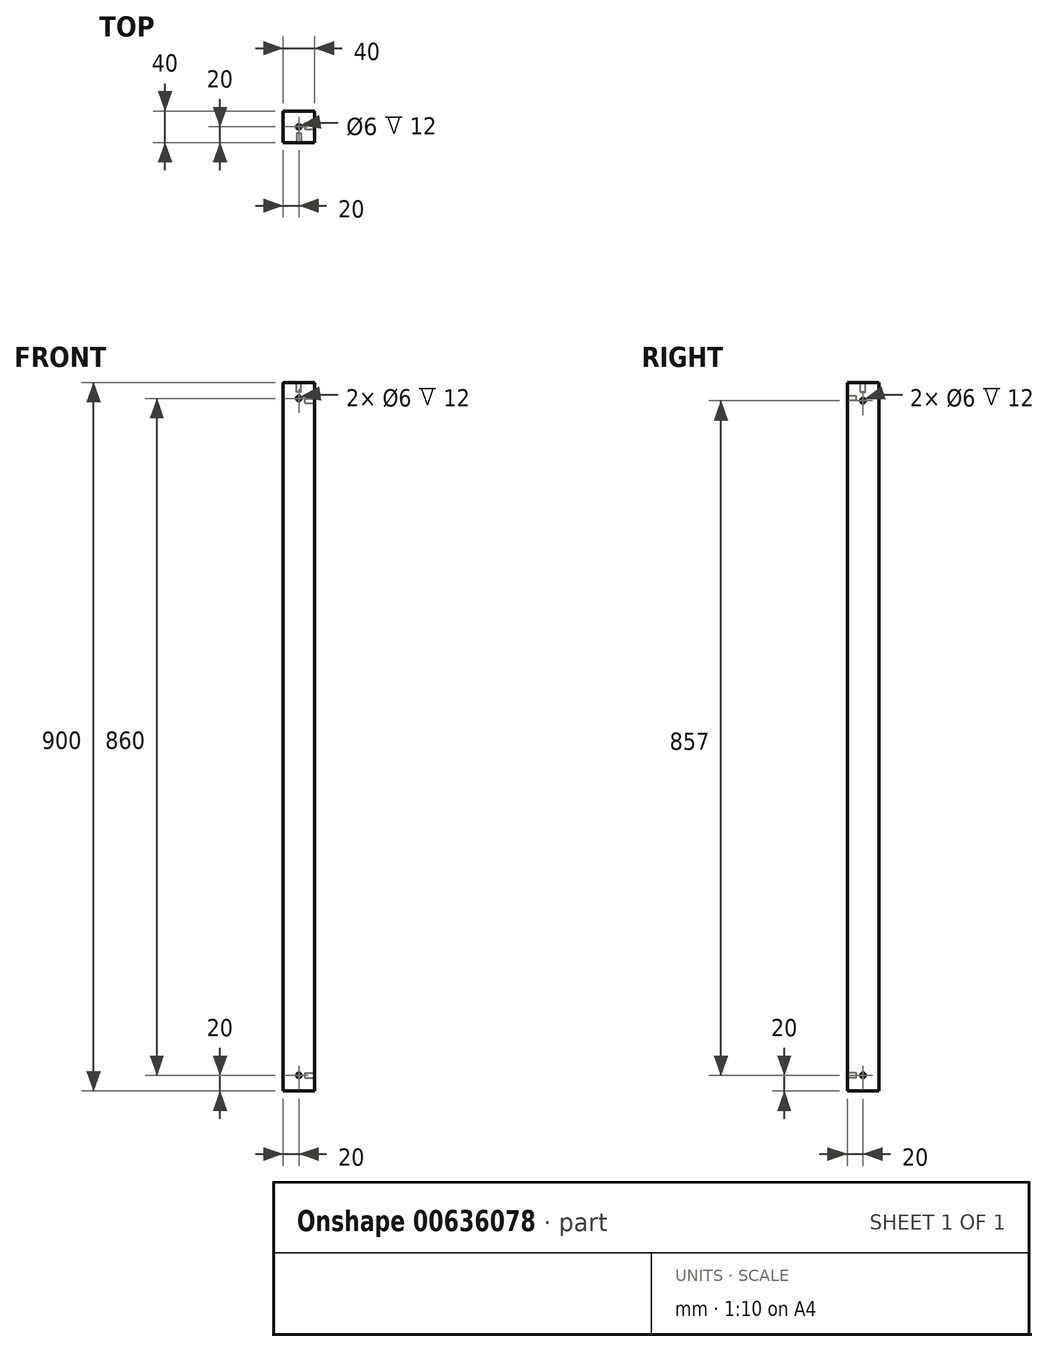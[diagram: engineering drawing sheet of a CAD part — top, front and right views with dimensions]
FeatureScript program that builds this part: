
annotation { "Feature Type Name" : "Feature", "Feature Type Description" : "" }
export const myFeature = defineFeature(function(context is Context, id is Id, definition is map)
    precondition{}
    {
        {
            var Q0;
            Q0=qCreatedBy(makeId("Top.planeOp"),FACE);
            var sketch = newSketch(context, id + "F0", { "sketchPlane" : qUnion([Q0])});
            skLineSegment(sketch, "E0.bottom", {"start": v(0, 0) * mm, "end": v(40, 0) * mm});
            skLineSegment(sketch, "E0.top", {"start": v(0, 40) * mm, "end": v(40, 40) * mm});
            skLineSegment(sketch, "E0.left", {"start": v(0, 0) * mm, "end": v(0, 40) * mm});
            skLineSegment(sketch, "E0.right", {"start": v(40, 0) * mm, "end": v(40, 40) * mm});
            skSolve(sketch);
        }
        {
            var Q0;
            Q0 = qSketchRegion(id + "F0", true);
            extrude(context, id + "F1", {"entities" : qUnion([Q0]), "depth" : 900 * mm, "offsetDistance" : 25 * mm});
        }
        {
            var Q0;
            Q0=makeQuery(id+"F1.opExtrude","CAP_FACE",FACE,{"disambiguationData":[OSD([sQuery(id+"F0.wireOp",EDGE,"E0.bottom"),sQuery(id+"F0.wireOp",EDGE,"E0.top"),sQuery(id+"F0.wireOp",EDGE,"E0.left"),sQuery(id+"F0.wireOp",EDGE,"E0.right")])],"isStart":false});
            var sketch = newSketch(context, id + "F2", { "sketchPlane" : qUnion([Q0])});
            skCircle(sketch, "E1", {"center": v(20, 20) * mm, "radius": 3 * mm});
            skSolve(sketch);
        }
        {
            var Q0;
            Q0 = qSketchRegion(id + "F2", true);
            extrude(context, id + "F3", {"entities" : qUnion([Q0]), "operationType" : NewBodyOperationType.REMOVE, "oppositeDirection" : true, "depth" : 12 * mm, "offsetDistance" : 25 * mm});
        }
        {
            var Q0;
            Q0=makeQuery(id+"F1.opExtrude","SWEPT_FACE",FACE,{"disambiguationData":[OSD([sQuery(id+"F0.wireOp",EDGE,"E0.bottom")])]});
            var sketch = newSketch(context, id + "F4", { "sketchPlane" : qUnion([Q0])});
            skCircle(sketch, "E2", {"center": v(20, 880) * mm, "radius": 3 * mm});
            skSolve(sketch);
        }
        {
            var Q0;
            Q0 = qSketchRegion(id + "F4", true);
            extrude(context, id + "F5", {"entities" : qUnion([Q0]), "operationType" : NewBodyOperationType.REMOVE, "oppositeDirection" : true, "depth" : 12 * mm, "offsetDistance" : 25 * mm});
        }
        {
            var Q0;
            Q0=makeQuery(id+"F1.opExtrude","SWEPT_FACE",FACE,{"disambiguationData":[OSD([sQuery(id+"F0.wireOp",EDGE,"E0.right")])]});
            var sketch = newSketch(context, id + "F6", { "sketchPlane" : qUnion([Q0])});
            skCircle(sketch, "E3", {"center": v(20, 877) * mm, "radius": 3 * mm});
            skSolve(sketch);
        }
        {
            var Q0;
            Q0 = qSketchRegion(id + "F6", true);
            extrude(context, id + "F7", {"entities" : qUnion([Q0]), "operationType" : NewBodyOperationType.REMOVE, "oppositeDirection" : true, "depth" : 12 * mm, "offsetDistance" : 25 * mm});
        }
        {
            var Q0;
            Q0=makeQuery(id+"F1.opExtrude","SWEPT_FACE",FACE,{"disambiguationData":[OSD([sQuery(id+"F0.wireOp",EDGE,"E0.right")])]});
            var sketch = newSketch(context, id + "F8", { "sketchPlane" : qUnion([Q0])});
            skCircle(sketch, "E4", {"center": v(20, 20) * mm, "radius": 3 * mm});
            skPoint(sketch, "E4.centerSnap0", {"position": v(20, 0) * mm});
            skSolve(sketch);
        }
        {
            var Q0;
            Q0 = qSketchRegion(id + "F8", true);
            extrude(context, id + "F9", {"entities" : qUnion([Q0]), "operationType" : NewBodyOperationType.REMOVE, "oppositeDirection" : true, "depth" : 12 * mm, "offsetDistance" : 25 * mm});
        }
        {
            var Q0;
            Q0=makeQuery(id+"F1.opExtrude","SWEPT_FACE",FACE,{"disambiguationData":[OSD([sQuery(id+"F0.wireOp",EDGE,"E0.bottom")])]});
            var sketch = newSketch(context, id + "F10", { "sketchPlane" : qUnion([Q0])});
            skCircle(sketch, "E5", {"center": v(20, 20) * mm, "radius": 3 * mm});
            skSolve(sketch);
        }
        {
            var Q0;
            Q0 = qSketchRegion(id + "F10", true);
            extrude(context, id + "F11", {"entities" : qUnion([Q0]), "operationType" : NewBodyOperationType.REMOVE, "oppositeDirection" : true, "depth" : 12 * mm, "offsetDistance" : 25 * mm});
        }
    });
